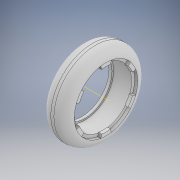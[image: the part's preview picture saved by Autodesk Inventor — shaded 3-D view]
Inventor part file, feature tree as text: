
AUTODESK INVENTOR PART (.ipt)
format: ipt  version: 2020 (Build 240168000, 168)  size: 229,888 bytes
history: native  units: mm
features: other x6, sketch x4, extrude x4, fillet x1, draft x1, pattern_circular x1
ambient origin geometry x8: Origin, YZ Plane, XZ Plane, XY Plane, X Axis, Y Axis, Z Axis, Center Point
bodies: Solid1 (feature_tree)
feature tree (17):
  sketch  "Sketch1"  dims[d0=27.5mm d1=19.0mm]
  sketch  "Sketch2"  dims[d2=5.0mm d3=21.0mm d4=6.0mm d5=0.0mm]
  extrude  "Extrusion1"  Depth=19.0mm
  extrude  "Extrusion2"  Depth=21.0mm
  fillet  "Fillet1"  Radius=6.0mm
  extrude  "Extrusion3"  Depth=3.5mm
  extrude  "Extrusion4"  Depth=1.0mm TaperAngle=0.0deg
  draft  "FaceDraft2"
  other  "Work Axis4"
  pattern_circular  "Circular Pattern1"  [2 undecoded]
  sketch  "Sketch3"  dims[d6=8.0mm d7=0.0mm d8=3.5mm]
  sketch  "Sketch4"  dims[d9=18.0mm d10=1.0mm d11=0.0mm d12=1.0mm d13=0.0mm d18=20.0mm d19=18.8mm d20=0.872665mm d21=60.0mm d22=360.0deg]
  other  "Work Axis5"
  other  "Work Axis6"
  other  "Work Axis7"
  other  "Work Axis8"
  other  "Work Axis9"
note: 2 required parameter values undecoded (feature->parameter linkage not recoverable at this tier; creation-order binding heuristic only, values carry confidence <= 0.55)
